# Revit family: Urinal-Washdown-Sloan-Top_Spud-SU-1209_Series
name_source: partatom
category: Plumbing Fixtures
revit_build: Autodesk Revit 2014 (Build: 20130308_1515(x64)
units: mm (PartAtom-declared; Revit-internal decimal feet)

## types (2) — shared parameters
Assembly Code = D2010210
CW Connection = Yes
CWFU = 5
Default Elevation = 17"
Fixture Color = Vitreous China-Sloan-White
Flush Choice = Single Flush
Flush Volumes and Flow Rates = 0.125 gpf to 0.5 gpf/0.5 Lpf to 1.9 Lpf
HW Connection = No
Inlet Spud Diameter = 3/4"
Inlet Spud Size = 3/4” I.P.S. top spud inlet
Manufacturer = Sloan
Mounting = Wall Hung
Product Documentation Link = https://specifications.sloan.com
Product URL = https://www.sloan.com
Revised Date = 10/7/2016
Spud Location = Top Spud
URL = http://www.sloan.com
Vent Connection = No
WFU = 5
Waste Connection = Yes
Waste Outlet Diameter = 2"

## per-type parameters (varying)
| type | Description | Order Code |
| SU-1209 | Complete HEU vitreous china retrofit top spud urinal fixture. | 1101209 |
| SU-1209-STG | Retrofit HE TS Urinal w/ SloanTec Glaze | 1171209 |

note: column(s) folded — value = type name in every type: Model

## geometry (parser evidence)
native form markers: Sweep x1
no freeform markers — native parametric forms only
